# Revit family: 6954 Стальной фонарный столб Т-12-3 со светильником Хоббика
name_source: partatom
category: Антураж
revit_build: Autodesk Revit 2018 (Build: 20180423_1000(x64)
units: mm (PartAtom-declared; Revit-internal decimal feet)

## family parameters
Всегда вертикально = Да
Источник визуального образа = Геометрия семейства
На основе рабочей плоскости = Нет
Общий = Нет
При загрузке вырезать с полостями = Нет
Точка расчета площади = Нет

## types (6) — shared parameters
URL = https://hobbyka.ru
Артикул товара = Арт. 6954
Группа модели = Светильники со стальными опорами
Длина = 1448 мм
Изготовитель = ООО «Хоббика»
Изображение типоразмера = Стальной фонарный столб Т-12-3 со светильником Арт 6954.jpg
Материал изделия = Сталь
Цвет каркаса = Сталь
Ширина = 400 мм

## per-type parameters (varying)
| type | Версия 3,661 м | Версия 4,161 м | Версия 4,661 м | Версия 5,161 м | Версия 5,661 м | Высота | Описание |
| Версия 3,661 м | Да | Нет | Нет | Нет | Нет | 3161 мм | Стальной фонарный столб Т-12-3 со светильником. Модель 3,661 м |
| Версия 4,161 м | Нет | Да | Нет | Нет | Нет | 4161 мм | Стальной фонарный столб Т-12-3 со светильником. Модель 4,161 м |
| Версия 4,661 м | Нет | Нет | Да | Нет | Нет | 4661 мм | Стальной фонарный столб Т-12-3 со светильником. Модель 4,661 м |
| Версия 5,161 м | Нет | Нет | Нет | Да | Нет | 5161 мм | Стальной фонарный столб Т-12-3 со светильником. Модель 5,161 м |
| Версия 5,661 м | Нет | Нет | Нет | Нет | Да | 5661 мм | Стальной фонарный столб Т-12-3 со светильником. Модель 5,661 м |
| Версия 6,161 м | Нет | Нет | Нет | Нет | Нет | 6161 мм | Стальной фонарный столб Т-12-3 со светильником. Модель 6,161 м |
